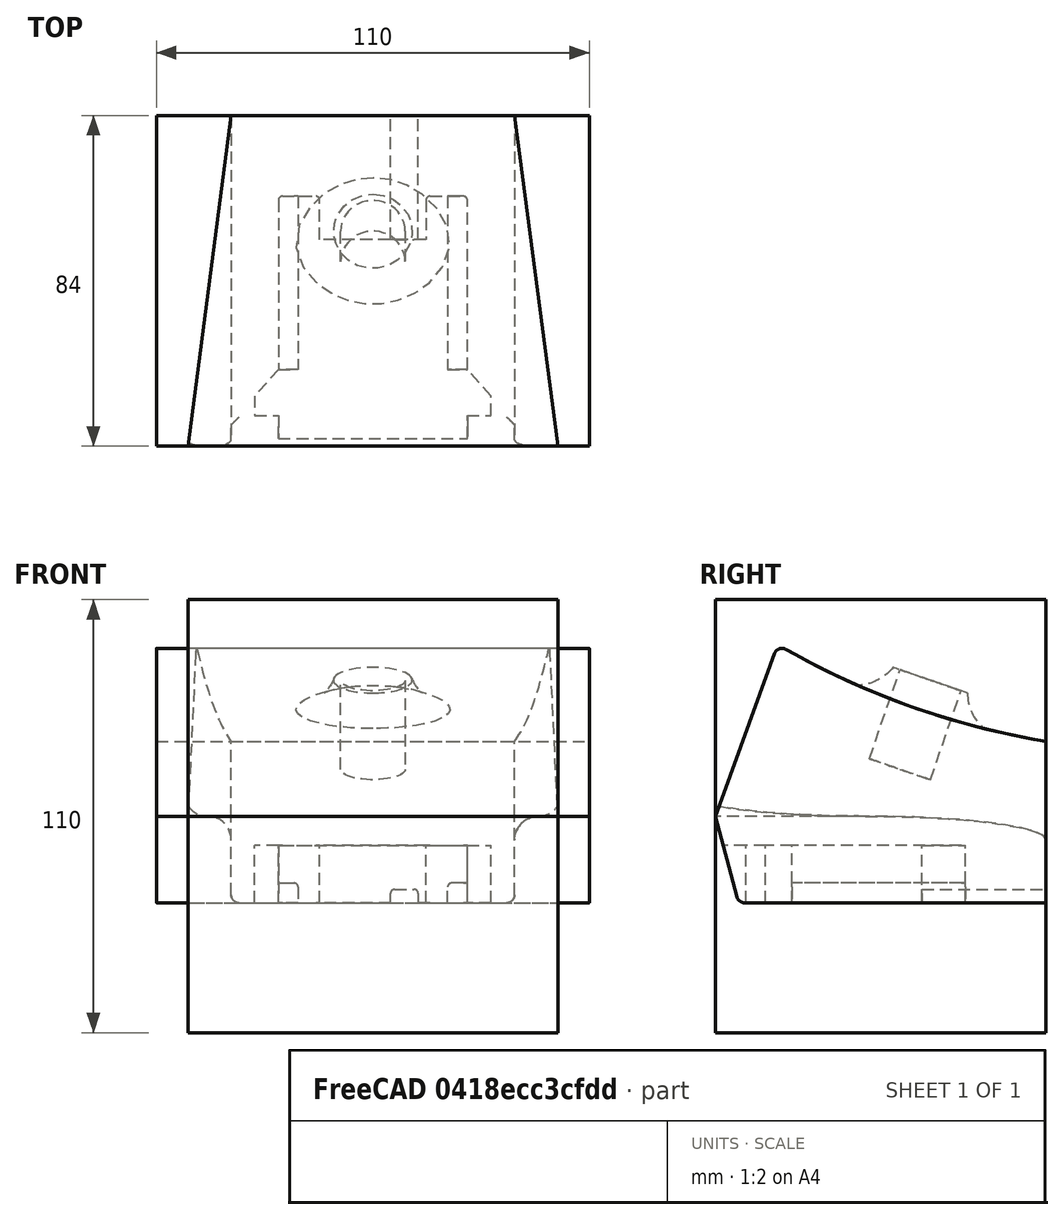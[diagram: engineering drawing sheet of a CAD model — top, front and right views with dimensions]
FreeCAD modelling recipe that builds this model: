
FCSTD DOCUMENT  (FreeCAD 0.19R24212 (Git))
Label: solder_station2
License: All rights reserved
LicenseURL: http://en.wikipedia.org/wiki/All_rights_reserved
objects: Sketcher::SketchObject×9, PartDesign::Pad×4, PartDesign::Body×3, PartDesign::Pocket×3, Spreadsheet::Sheet×1, Mesh::Feature×1, PartDesign::Boolean×1, PartDesign::Revolution×1, App::Part×1
note: 29 computed .brp shape members not serialized (recipe doc carries the construction recipe); baked Part::Feature solids carry a one-line shape summary decoded from their .brp

FEATURE [Sketcher::SketchObject] Sketch  label="RearSupport"
  AttachmentOffset = pos=(0,0,-42) rot=(0,0,1;0rad)
  FullyConstrained = true
  MapMode = 5
  Placement = pos=(-42,9.3e-15,-9.3e-15) rot=(0.57735,0.57735,0.57735;2.0944rad)
  Support = -> [YZ_Plane]
  expr: Constraints[44] = 3
  expr: Constraints[16] = <<param>>.rear_width
  expr: Constraints[52] = <<param>>.wall * 2
  expr: Constraints[56] = <<param>>.wall * 2
  expr: Constraints[15] = Spreadsheet.radius_big
  expr: .AttachmentOffset.Base.z = -Spreadsheet.mid_depth / 2
  expr: Constraints[18] = <<param>>.rear_height
  expr: Constraints[17] = <<param>>.rear_width / 2
  expr: Constraints[55] = <<param>>.wall * 2
  expr: Constraints[53] = <<param>>.wall * 2
  expr: Constraints[54] = <<param>>.wall * 2
  expr: Constraints[57] = <<param>>.wall * 2
  sketch-geometry (24):
    g0: LineSegment StartX=-30 StartY=41 StartZ=0 EndX=30 EndY=41 EndZ=0
    g1: LineSegment StartX=36 StartY=35 StartZ=0 EndX=36 EndY=6 EndZ=0
    g2: LineSegment StartX=30 StartY=0 StartZ=0 EndX=-30 EndY=0 EndZ=0
    g3: LineSegment StartX=-36 StartY=6 StartZ=0 EndX=-36 EndY=35 EndZ=0
    g4: ArcOfCircle CenterX=-30 CenterY=35 CenterZ=0 NormalX=0 NormalY=0 NormalZ=1 AngleXU=0 Radius=6 StartAngle=1.5708 EndAngle=3.14159
    g5: ArcOfCircle CenterX=30 CenterY=35 CenterZ=0 NormalX=0 NormalY=0 NormalZ=1 AngleXU=0 Radius=6 StartAngle=-9e-16 EndAngle=1.5708
    g6: ArcOfCircle CenterX=30 CenterY=6 CenterZ=0 NormalX=0 NormalY=0 NormalZ=1 AngleXU=0 Radius=6 StartAngle=4.71239 EndAngle=6.28319
    g7: ArcOfCircle CenterX=-30 CenterY=6 CenterZ=0 NormalX=0 NormalY=0 NormalZ=1 AngleXU=0 Radius=6 StartAngle=3.14159 EndAngle=4.71239
    g8: LineSegment StartX=-26.6 StartY=34.6 StartZ=0 EndX=-9.4 EndY=34.6 EndZ=0
    g9: LineSegment StartX=29.6 StartY=31.6 StartZ=0 EndX=29.6 EndY=9.4 EndZ=0
    g10: LineSegment StartX=26.6 StartY=6.4 StartZ=0 EndX=9.4 EndY=6.4 EndZ=0
    g11: LineSegment StartX=-29.6 StartY=9.4 StartZ=0 EndX=-29.6 EndY=31.6 EndZ=0
    g12: LineSegment StartX=-6.4 StartY=31.6 StartZ=0 EndX=-6.4 EndY=9.4 EndZ=0
    g13: LineSegment StartX=6.4 StartY=31.6 StartZ=0 EndX=6.4 EndY=9.4 EndZ=0
    g14: LineSegment StartX=9.4 StartY=34.6 StartZ=0 EndX=26.6 EndY=34.6 EndZ=0
    g15: LineSegment StartX=-9.4 StartY=6.4 StartZ=0 EndX=-26.6 EndY=6.4 EndZ=0
    g16: ArcOfCircle CenterX=-9.4 CenterY=31.6 CenterZ=0 NormalX=0 NormalY=0 NormalZ=1 AngleXU=0 Radius=3 StartAngle=4e-16 EndAngle=1.5708
    g17: ArcOfCircle CenterX=9.4 CenterY=31.6 CenterZ=0 NormalX=0 NormalY=0 NormalZ=1 AngleXU=0 Radius=3 StartAngle=1.5708 EndAngle=3.14159
    g18: ArcOfCircle CenterX=-9.4 CenterY=9.4 CenterZ=0 NormalX=0 NormalY=0 NormalZ=1 AngleXU=0 Radius=3 StartAngle=4.71239 EndAngle=6.28319
    g19: ArcOfCircle CenterX=9.4 CenterY=9.4 CenterZ=0 NormalX=0 NormalY=0 NormalZ=1 AngleXU=0 Radius=3 StartAngle=3.14159 EndAngle=4.71239
    g20: ArcOfCircle CenterX=-26.6 CenterY=31.6 CenterZ=0 NormalX=0 NormalY=0 NormalZ=1 AngleXU=0 Radius=3 StartAngle=1.5708 EndAngle=3.14159
    g21: ArcOfCircle CenterX=-26.6 CenterY=9.4 CenterZ=0 NormalX=0 NormalY=0 NormalZ=1 AngleXU=0 Radius=3 StartAngle=3.14159 EndAngle=4.71239
    g22: ArcOfCircle CenterX=26.6 CenterY=31.6 CenterZ=0 NormalX=0 NormalY=0 NormalZ=1 AngleXU=0 Radius=3 StartAngle=2e-16 EndAngle=1.5708
    g23: ArcOfCircle CenterX=26.6 CenterY=9.4 CenterZ=0 NormalX=0 NormalY=0 NormalZ=1 AngleXU=0 Radius=3 StartAngle=4.71239 EndAngle=6.28319
  constraints (58):
    c: Horizontal(g0)
    c: Horizontal(g2)
    c: Vertical(g1)
    c: Vertical(g3)
    c: Tangent(g3,g4) = 1.5708
    c: Tangent(g0,g4) = 1.5708
    c: Tangent(g0,g5) = 1.5708
    c: Tangent(g1,g5) = 1.5708
    c: Tangent(g1,g6) = 1.5708
    c: Tangent(g2,g6) = 1.5708
    c: Tangent(g2,g7) = 1.5708
    c: Tangent(g3,g7) = 1.5708
    c: Equal(g4,g7)
    c: Equal(g7,g6)
    c: Equal(g6,g5)
    c: Radius(g4) = 6
    c: DistanceX(g3,g1) = 72
    c: DistanceX(g3,g-1) = 36
    c: DistanceY(g2,g0) = 41
    c: Horizontal(g8)
    c: Horizontal(g10)
    c: Vertical(g9)
    c: Vertical(g11)
    c: Vertical(g12)
    c: Vertical(g13)
    c: PointOnObject(g-1,g2)
    c: Tangent(g8,g14)
    c: Tangent(g10,g15)
    c: Tangent(g8,g16) = 1.5708
    c: Tangent(g12,g16) = 1.5708
    c: Tangent(g13,g17) = -1.5708
    c: Tangent(g14,g17) = 1.5708
    c: Tangent(g15,g18) = 1.5708
    c: Tangent(g12,g18) = 1.5708
    c: Tangent(g13,g19) = -1.5708
    c: Tangent(g10,g19) = 1.5708
    c: Tangent(g8,g20) = 1.5708
    c: Tangent(g11,g20) = 1.5708
    c: Tangent(g11,g21) = 1.5708
    c: Tangent(g15,g21) = 1.5708
    c: Tangent(g14,g22) = 1.5708
    c: Tangent(g9,g22) = 1.5708
    c: Tangent(g9,g23) = 1.5708
    c: Tangent(g10,g23) = 1.5708
    c: Radius(g17) = 3
    c: Equal(g20,g21)
    c: Equal(g21,g18)
    c: Equal(g18,g16)
    c: Equal(g16,g19)
    c: Equal(g19,g23)
    c: Equal(g23,g22)
    c: Equal(g22,g17)
    c: DistanceY(g-1,g15) = 6.4
    c: DistanceX(g3,g11) = 6.4
    c: DistanceX(g9,g1) = 6.4
    c: DistanceX(g12,g-1) = 6.4
    c: DistanceX(g-1,g13) = 6.4
    c: DistanceY(g14,g0) = 6.4
FEATURE [Spreadsheet::Sheet] Spreadsheet  label="param"
  cells = A1=Body; B2=top_depth; C2(top_depth)=70; B3=mid_depth; C3(mid_depth)=84; B4=bottom_depth; C4(bottom_depth)=75; B6=bottom_width; C6(bottom_width)=72; B7=bottom_height; C7(bottom_height)=22; B8=bottom_angle; C8(bottom_angle)=15; B10=rear_width; C10(rear_width)=72; B11=rear_height; C11(rear_height)=41; B13=center_width; C13(center_width)=80; B14=center_height; C14(center_height)=50; B16=front_width1; C16(front_width1)=91; D16=@top; E16=not used; B17=front_width2; C17(front_width2)=94; D17=@mid; B18=front_height; C18(front_height)=65; B19=front_wall; C19(front_wall)=5; B20=front_face; C20(front_face)=44; B21=front_angle; C21(front_angle)=20; B23=wall; C23(wall)=3.2; B24=radius_big; C24(radius_big)=6; B25=radius_small; C25(radius_small)=2; B26=arch; C26(arch)=200; A28=Button; B29=button_offset; C29(button_offset)=10; B30=button_inside_dia; C30(button_inside_dia)=20; B31=button_outside_dia; C31(button_outside_dia)=40; B32=button_height; C32(button_height)=27; B33=button_extension; C33(button_extension)=8; B34=button_fillet; C34(button_fillet)=12; B35=button_angle; C35(button_angle)=-19; B36=button_hole; C36(button_hole)=16.4; B37=button_hole_center; C37(button_hole_center)=-0.5; A38=Battery Cuts; B39=batt_carveout; C39(batt_carveout)=14.6; B40=batt_rail; C40(batt_rail)=5; B41=batt_rail_length; C41(batt_rail_length)=44; A43=Terminals; B44=terminal_width; B45=terminal_height; A47=Box Interior
FEATURE [Sketcher::SketchObject] Sketch008  label="SketchButtonHole"
  AttachmentOffset = pos=(0,-0.5,27) rot=(1,0,0;-0.331613rad)
  FullyConstrained = true
  MapMode = 5
  Placement = pos=(0,-0.5,27) rot=(1,0,0;5.95157rad)
  Support = -> [XY_Plane004]
  expr: .AttachmentOffset.Base.z = <<param>>.button_height
  expr: Constraints[0] = <<param>>.button_hole
  expr: .AttachmentOffset.Base.y = <<param>>.button_hole_center
  expr: .AttachmentOffset.Rotation.Angle = <<param>>.button_angle
  expr: Constraints[2] = <<param>>.button_offset
  sketch-geometry (1):
    g0: Circle CenterX=0 CenterY=10 CenterZ=0 NormalX=0 NormalY=0 NormalZ=1 AngleXU=0 Radius=8.2
  constraints (3):
    c: Diameter(g0) = 16.4
    c: PointOnObject(g0,g-2)
    c: DistanceY(g-1,g0) = 10
FEATURE [Mesh::Feature] M18_soldering_case
  Placement = pos=(48,-41,-22) rot=(0,0.707107,0.707107;3.14159rad)
FEATURE [Sketcher::SketchObject] Sketch012  label="SketchSide"
  FullyConstrained = true
  MapMode = 5
  Placement = pos=(0,0,0) rot=(0.57735,0.57735,0.57735;2.0944rad)
  Support = -> [YZ_Plane002]
  expr: Constraints[21] = 90 - <<param>>.bottom_angle
  expr: Constraints[20] = <<param>>.radius_small
  expr: Constraints[19] = <<param>>.bottom_height
  expr: Constraints[8] = <<param>>.arch
  expr: Constraints[6] = <<param>>.rear_height - <<param>>.bottom_height
  expr: Constraints[11] = <<param>>.front_face
  expr: Constraints[7] = <<param>>.radius_small
  expr: Constraints[22] = 90 - <<param>>.front_angle
  expr: Constraints[9] = <<param>>.mid_depth
  sketch-geometry (8):
    g0: LineSegment StartX=42 StartY=0 StartZ=0 EndX=42 EndY=19 EndZ=0
    g1: LineSegment StartX=-42 StartY=0 StartZ=0 EndX=-26.9511 EndY=41.3465 EndZ=0
    g2: ArcOfCircle CenterX=-25.0717 CenterY=40.6624 CenterZ=0 NormalX=0 NormalY=0 NormalZ=1 AngleXU=0 Radius=2 StartAngle=1.05429 EndAngle=2.79253
    g3: ArcOfCircle CenterX=74.6859 CenterY=216.311 CenterZ=0 NormalX=0 NormalY=0 NormalZ=1 AngleXU=0 Radius=200 StartAngle=4.19588 EndAngle=4.54822
    g4: LineSegment StartX=-42 StartY=0 StartZ=0 EndX=-36.5023 EndY=-20.5176 EndZ=0
    g5: LineSegment StartX=-34.5705 StartY=-22 StartZ=0 EndX=42 EndY=-22 EndZ=0
    g6: LineSegment StartX=42 StartY=-22 StartZ=0 EndX=42 EndY=0 EndZ=0
    g7: ArcOfCircle CenterX=-34.5705 CenterY=-20 CenterZ=0 NormalX=0 NormalY=0 NormalZ=1 AngleXU=0 Radius=2 StartAngle=3.4034 EndAngle=4.71239
  constraints (25):
    c: PointOnObject(g1,g-1)
    c: Vertical(g0)
    c: Coincident(g2,g1)
    c: Coincident(g3,g0)
    c: Tangent(g3,g2) = 1.5708
    c: Symmetric(g1,g0,g-2)
    c: DistanceY(g0,g0) = 19
    c: Radius(g2) = 2
    c: Radius(g3) = 200
    c: DistanceX(g1,g0) = 84
    c: Tangent(g2,g1)
    c: Distance(g1) = 44
    c: Horizontal(g5)
    c: Coincident(g6,g5)
    c: Vertical(g6)
    c: Coincident(g7,g4)
    c: Coincident(g7,g5)
    c: Tangent(g7,g5)
    c: Tangent(g7,g4)
    c: DistanceY(g5,g-1) = 22
    c: Radius(g7) = 2
    c: Angle(g4,g-1) = 1.309
    c: Angle(g-1,g1) = 1.22173
    c: Coincident(g4,g1)
    c: Coincident(g6,g0)
FEATURE [PartDesign::Pad] Pad  label="PadSide"
  Direction = (1,1,1)
  Length = 110
  Length2 = 100
  Midplane = true
  Placement = pos=(0,0,0) rot=(0.57735,0.57735,0.57735;2.0944rad)
  Profile = -> Sketch012
  Type = 0
FEATURE [PartDesign::Body] Body001  label="BodySide"
  Group = -> [Sketch012,Pad]
  Origin = -> Origin002
  Tip = -> Pad
FEATURE [Sketcher::SketchObject] Sketch013  label="SketchTop"
  FullyConstrained = true
  MapMode = 5
  Support = -> [XY_Plane003]
  expr: Constraints[4] = <<param>>.front_width2
  expr: Constraints[6] = <<param>>.rear_width
  expr: Constraints[8] = <<param>>.mid_depth
  expr: Constraints[9] = <<param>>.mid_depth / 2
  sketch-geometry (4):
    g0: LineSegment StartX=36 StartY=42 StartZ=0 EndX=-36 EndY=42 EndZ=0
    g1: LineSegment StartX=-36 StartY=42 StartZ=0 EndX=-47 EndY=-42 EndZ=0
    g2: LineSegment StartX=-47 StartY=-42 StartZ=0 EndX=47 EndY=-42 EndZ=0
    g3: LineSegment StartX=47 StartY=-42 StartZ=0 EndX=36 EndY=42 EndZ=0
  constraints (10):
    c: Coincident(g0,g1)
    c: Coincident(g1,g2)
    c: Coincident(g2,g3)
    c: Coincident(g3,g0)
    c: DistanceX(g1,g2) = 94
    c: Symmetric(g2,g1,g-2)
    c: DistanceX(g0,g0) = 72
    c: Symmetric(g0,g0,g-2)
    c: DistanceY(g2,g0) = 84
    c: DistanceY(g2,g-1) = 42
FEATURE [PartDesign::Pad] Pad001  label="PadTop"
  Direction = (1,1,1)
  Length = 110
  Length2 = 100
  Midplane = true
  Profile = -> Sketch013
  Type = 0
FEATURE [PartDesign::Body] Body002  label="BodyTop"
  Group = -> [Sketch013,Pad001]
  Origin = -> Origin003
  Tip = -> Pad001
FEATURE [Sketcher::SketchObject] Sketch017  label="SketchFront"
  FullyConstrained = true
  MapMode = 5
  Placement = pos=(0,0,0) rot=(1,0,0;1.5708rad)
  Support = -> [XZ_Plane004]
  expr: Constraints[37] = <<param>>.front_height
  expr: Constraints[35] = <<param>>.front_width2
  expr: Constraints[34] = <<param>>.front_width1
  expr: Constraints[33] = <<param>>.bottom_width
  expr: Constraints[38] = <<param>>.bottom_height
  expr: Constraints[29] = <<param>>.radius_big
  expr: Constraints[28] = <<param>>.radius_small
  sketch-geometry (12):
    g0: LineSegment StartX=-34 StartY=-22 StartZ=0 EndX=34 EndY=-22 EndZ=0
    g1: LineSegment StartX=36 StartY=-20 StartZ=0 EndX=36 EndY=-6.00003 EndZ=0
    g2: LineSegment StartX=-36 StartY=-20 StartZ=0 EndX=-36 EndY=-6 EndZ=0
    g3: ArcOfCircle CenterX=-42 CenterY=-6 CenterZ=0 NormalX=0 NormalY=0 NormalZ=1 AngleXU=0 Radius=6 StartAngle=3.32288e-09 EndAngle=1.5708
    g4: ArcOfCircle CenterX=42 CenterY=-6 CenterZ=0 NormalX=0 NormalY=0 NormalZ=1 AngleXU=0 Radius=6 StartAngle=1.5708 EndAngle=3.1416
    g5: ArcOfCircle CenterX=42 CenterY=6 CenterZ=0 NormalX=0 NormalY=0 NormalZ=1 AngleXU=0 Radius=6 StartAngle=4.71239 EndAngle=5.6975
    g6: ArcOfCircle CenterX=-42 CenterY=6 CenterZ=0 NormalX=0 NormalY=0 NormalZ=1 AngleXU=0 Radius=6 StartAngle=3.72728 EndAngle=4.71239
    g7: LineSegment StartX=47 StartY=2.68339 StartZ=0 EndX=45.5 EndY=43 EndZ=0
    g8: LineSegment StartX=-45.5 StartY=43 StartZ=0 EndX=45.5 EndY=43 EndZ=0
    g9: ArcOfCircle CenterX=34 CenterY=-20 CenterZ=0 NormalX=0 NormalY=0 NormalZ=1 AngleXU=0 Radius=2 StartAngle=4.71239 EndAngle=6.28319
    g10: ArcOfCircle CenterX=-34 CenterY=-20 CenterZ=0 NormalX=0 NormalY=0 NormalZ=1 AngleXU=0 Radius=2 StartAngle=3.14159 EndAngle=4.71239
    g11: LineSegment StartX=-45.5 StartY=43 StartZ=0 EndX=-47 EndY=2.68339 EndZ=0
  constraints (39):
    c: Coincident(g8,g11)
    c: Coincident(g8,g7)
    c: Coincident(g11,g6)
    c: Coincident(g5,g7)
    c: Coincident(g0,g9)
    c: Coincident(g9,g1)
    c: Coincident(g0,g10)
    c: Coincident(g2,g10)
    c: Coincident(g2,g3)
    c: Coincident(g4,g1)
    c: Coincident(g4,g5)
    c: Coincident(g6,g3)
    c: Vertical(g1)
    c: Vertical(g2)
    c: PointOnObject(g4,g-1)
    c: Symmetric(g4,g3,g-2)
    c: Symmetric(g0,g0,g-2)
    c: Symmetric(g7,g8,g-2)
    c: Tangent(g9,g0)
    c: Tangent(g9,g1)
    c: Tangent(g10,g0)
    c: Tangent(g10,g2)
    c: Tangent(g3,g2)
    c: Tangent(g4,g1)
    c: Equal(g3,g6)
    c: Equal(g6,g4)
    c: Equal(g4,g5)
    c: Equal(g9,g10)
    c: Radius(g9) = 2
    c: Radius(g4) = 6
    c: Tangent(g4,g5)
    c: Tangent(g3,g6)
    c: Vertical(g4,g4)
    c: DistanceX(g2,g1) = 72
    c: DistanceX(g8,g8) = 91
    c: DistanceX(g6,g5) = 94
    c: Equal(g11,g7)
    c: DistanceY(g0,g7) = 65
    c: DistanceY(g0,g4) = 22
FEATURE [PartDesign::Pad] Pad003  label="PadFront"
  Direction = (1,1,1)
  Length = 110
  Length2 = 100
  Midplane = true
  Placement = pos=(0,0,0) rot=(1,0,0;1.5708rad)
  Profile = -> Sketch017
  Type = 0
FEATURE [PartDesign::Boolean] Boolean
  BaseFeature = -> Pad003
  Group = -> [Body002,Body001]
  Type = 2
FEATURE [Sketcher::SketchObject] Sketch018  label="SketchBat1"
  AttachmentOffset = pos=(0,0,-22) rot=(0,0,1;0rad)
  FullyConstrained = true
  MapMode = 5
  Placement = pos=(0,0,-22) rot=(0,0,1;0rad)
  Support = -> [XY_Plane004]
  expr: .AttachmentOffset.Base.z = -<<param>>.bottom_height
  sketch-geometry (21):
    g0: LineSegment StartX=-24 StartY=-44.2082 StartZ=0 EndX=24 EndY=-44.2082 EndZ=0
    g1: LineSegment StartX=24 StartY=-44.2082 StartZ=0 EndX=24 EndY=-34.2082 EndZ=0
    g2: LineSegment StartX=24 StartY=-34.2082 StartZ=0 EndX=30 EndY=-34.2082 EndZ=0
    g3: LineSegment StartX=30 StartY=-34.2082 StartZ=0 EndX=30 EndY=-29.2082 EndZ=0
    g4: LineSegment StartX=30 StartY=-29.2082 StartZ=0 EndX=24 EndY=-22.5 EndZ=0
    g5: LineSegment StartX=24 StartY=-22.5 StartZ=0 EndX=24 EndY=20.5 EndZ=0
    g6: LineSegment StartX=13.5 StartY=20.5 StartZ=0 EndX=13.5 EndY=10.5 EndZ=0
    g7: LineSegment StartX=13.5 StartY=10.5 StartZ=0 EndX=-13.5 EndY=10.5 EndZ=0
    g8: LineSegment StartX=-13.5 StartY=10.5 StartZ=0 EndX=-13.5 EndY=20.5 EndZ=0
    g9: LineSegment StartX=-24 StartY=20.5 StartZ=0 EndX=-24 EndY=-22.5 EndZ=0
    g10: LineSegment StartX=-24 StartY=-22.5 StartZ=0 EndX=-30 EndY=-29.2082 EndZ=0
    g11: LineSegment StartX=-30 StartY=-29.2082 StartZ=0 EndX=-30 EndY=-34.2082 EndZ=0
    g12: LineSegment StartX=-30 StartY=-34.2082 StartZ=0 EndX=-24 EndY=-34.2082 EndZ=0
    g13: LineSegment StartX=-24 StartY=-34.2082 StartZ=0 EndX=-24 EndY=-44.2082 EndZ=0
    g14: Circle CenterX=0 CenterY=37.5 CenterZ=0 NormalX=0 NormalY=0 NormalZ=1 AngleXU=0 Radius=4
    g15: ArcOfCircle CenterX=-14.5 CenterY=20.5 CenterZ=0 NormalX=0 NormalY=0 NormalZ=1 AngleXU=0 Radius=1 StartAngle=4.17262e-08 EndAngle=1.5708
    g16: LineSegment StartX=-23 StartY=21.5 StartZ=0 EndX=-14.5 EndY=21.5 EndZ=0
    g17: LineSegment StartX=14.5 StartY=21.5 StartZ=0 EndX=23 EndY=21.5 EndZ=0
    g18: ArcOfCircle CenterX=-23 CenterY=20.5 CenterZ=0 NormalX=0 NormalY=0 NormalZ=1 AngleXU=0 Radius=1 StartAngle=1.5708 EndAngle=3.14159
    g19: ArcOfCircle CenterX=14.5 CenterY=20.5 CenterZ=0 NormalX=0 NormalY=0 NormalZ=1 AngleXU=0 Radius=1 StartAngle=1.5708 EndAngle=3.14159
    g20: ArcOfCircle CenterX=23 CenterY=20.5 CenterZ=0 NormalX=0 NormalY=0 NormalZ=1 AngleXU=0 Radius=0.999999 StartAngle=6.28318 EndAngle=7.85398
  constraints (65):
    c: Horizontal(g0)
    c: Coincident(g1,g0)
    c: Vertical(g1)
    c: Coincident(g2,g1)
    c: Horizontal(g2)
    c: Coincident(g3,g2)
    c: Coincident(g3,g4)
    c: Vertical(g5)
    c: Coincident(g6,g7)
    c: Coincident(g7,g8)
    c: Vertical(g8)
    c: Vertical(g9)
    c: Coincident(g10,g11)
    c: Vertical(g11)
    c: Coincident(g11,g12)
    c: Horizontal(g12)
    c: Coincident(g12,g13)
    c: Equal(g6,g8)
    c: Equal(g5,g9)
    c: Equal(g4,g10)
    c: Equal(g3,g11)
    c: Equal(g12,g2)
    c: Equal(g1,g13)
    c: Coincident(g13,g0)
    c: Vertical(g13)
    c: DistanceX(g7,g7) = 27
    c: Symmetric(g7,g6,g-2)
    c: Distance(g4) = 9
    c: Vertical(g3)
    c: DistanceY(g3,g3) = 5
    c: DistanceX(g2,g2) = 6
    c: DistanceY(g1,g1) = 10
    c: DistanceX(g0,g0) = 48
    c: PointOnObject(g14,g-2)
    c: Coincident(g9,g10)
    c: Coincident(g5,g4)
    c: Coincident(g15,g8)
    c: Coincident(g16,g15)
    c: Tangent(g15,g8)
    c: Horizontal(g16)
    c: Horizontal(g17)
    c: DistanceX(g9,g5) = 48
    c: Symmetric(g4,g9,g-2)
    c: Equal(g16,g17)
    c: Coincident(g18,g9)
    c: Coincident(g18,g16)
    c: Equal(g18,g15)
    c: Tangent(g18,g16)
    c: Tangent(g18,g9)
    c: DistanceY(g6,g17) = 11
    c: Vertical(g6)
    c: Coincident(g19,g6)
    c: Coincident(g19,g17)
    c: Coincident(g20,g17)
    c: Coincident(g20,g5)
    c: Tangent(g20,g17)
    c: Tangent(g20,g5)
    c: Tangent(g19,g6)
    c: Tangent(g19,g17)
    c: Equal(g15,g19)
    c: Radius(g19) = 1
    c: Radius(g14) = 4
    c: DistanceY(g15,g14) = 16
    c: DistanceY(g9,g16) = 44
    c: DistanceY(g-1,g14) = 37.5
FEATURE [PartDesign::Pocket] Pocket  label="PocketBatt"
  BaseFeature = -> Boolean
  Length = 14.6
  Length2 = 100
  Profile = -> Sketch018
  Reversed = true
  Type = 0
  expr: Length = Spreadsheet.batt_carveout
FEATURE [Sketcher::SketchObject] Sketch019  label="SketchBat2"
  AttachmentOffset = pos=(0,0,-21.5) rot=(0,0,1;0rad)
  FullyConstrained = true
  MapMode = 5
  Placement = pos=(0,21.5,4.8e-15) rot=(1,0,0;1.5708rad)
  Support = -> [XZ_Plane004]
  expr: Constraints[28] = 48.01mm
  expr: .AttachmentOffset.Base.z = -<<param>>.bottom_depth / 2 + 16
  expr: Constraints[26] = <<param>>.bottom_height
  expr: Constraints[29] = <<param>>.batt_rail
  expr: Constraints[27] = <<param>>.batt_rail
  sketch-geometry (10):
    g0: LineSegment StartX=-24.005 StartY=-17 StartZ=0 EndX=-20.005 EndY=-17 EndZ=0
    g1: LineSegment StartX=-19.005 StartY=-22 StartZ=0 EndX=-24.005 EndY=-22 EndZ=0
    g2: LineSegment StartX=-24.005 StartY=-22 StartZ=0 EndX=-24.005 EndY=-17 EndZ=0
    g3: LineSegment StartX=24.005 StartY=-17 StartZ=0 EndX=20.005 EndY=-17 EndZ=0
    g4: LineSegment StartX=19.005 StartY=-22 StartZ=0 EndX=24.005 EndY=-22 EndZ=0
    g5: LineSegment StartX=24.005 StartY=-22 StartZ=0 EndX=24.005 EndY=-17 EndZ=0
    g6: LineSegment StartX=-19.005 StartY=-18 StartZ=0 EndX=-19.005 EndY=-22 EndZ=0
    g7: ArcOfCircle CenterX=20.005 CenterY=-18 CenterZ=0 NormalX=0 NormalY=0 NormalZ=1 AngleXU=0 Radius=1 StartAngle=1.5708 EndAngle=3.1416
    g8: LineSegment StartX=19.005 StartY=-22 StartZ=0 EndX=19.005 EndY=-18 EndZ=0
    g9: ArcOfCircle CenterX=-20.005 CenterY=-18 CenterZ=0 NormalX=0 NormalY=0 NormalZ=1 AngleXU=0 Radius=1 StartAngle=6.28318 EndAngle=7.85398
  constraints (30):
    c: Coincident(g1,g2)
    c: Coincident(g2,g0)
    c: Horizontal(g0)
    c: Horizontal(g1)
    c: Vertical(g2)
    c: Coincident(g4,g5)
    c: Coincident(g5,g3)
    c: Horizontal(g3)
    c: Horizontal(g4)
    c: Vertical(g5)
    c: Coincident(g6,g1)
    c: Vertical(g6)
    c: Equal(g1,g4)
    c: Tangent(g3,g7) = -1.5708
    c: Coincident(g8,g4)
    c: Vertical(g8)
    c: Coincident(g7,g8)
    c: Coincident(g9,g0)
    c: Coincident(g9,g6)
    c: Equal(g6,g8)
    c: Tangent(g7,g8)
    c: Tangent(g9,g6)
    c: Tangent(g9,g0)
    c: Equal(g9,g7)
    c: Radius(g9) = 1
    c: Symmetric(g1,g4,g-2)
    c: DistanceY(g1,g-1) = 22
    c: DistanceY(g4,g3) = 5
    c: DistanceX(g1,g4) = 48.01
    c: DistanceX(g4,g4) = 5
FEATURE [PartDesign::Pad] Pad004  label="PadRail"
  BaseFeature = -> Pocket
  Direction = (1,1,1)
  Length = 44
  Length2 = 100
  Profile = -> Sketch019
  Type = 0
  expr: Length = <<param>>.batt_rail_length
FEATURE [Sketcher::SketchObject] Sketch020  label="SketchNotch"
  FullyConstrained = true
  MapMode = 5
  Placement = pos=(0,0,0) rot=(1,0,0;1.5708rad)
  Support = -> [XZ_Plane004]
  expr: Constraints[6] = <<param>>.bottom_height
  sketch-geometry (6):
    g0: LineSegment StartX=5.5 StartY=-18.6 StartZ=0 EndX=10.5 EndY=-18.6 EndZ=0
    g1: LineSegment StartX=11.5 StartY=-19.6 StartZ=0 EndX=11.5 EndY=-22 EndZ=0
    g2: LineSegment StartX=11.5 StartY=-22 StartZ=0 EndX=4.5 EndY=-22 EndZ=0
    g3: LineSegment StartX=4.5 StartY=-22 StartZ=0 EndX=4.5 EndY=-19.6 EndZ=0
    g4: ArcOfCircle CenterX=5.5 CenterY=-19.6 CenterZ=0 NormalX=0 NormalY=0 NormalZ=1 AngleXU=0 Radius=1 StartAngle=1.5708 EndAngle=3.14159
    g5: ArcOfCircle CenterX=10.5 CenterY=-19.6 CenterZ=0 NormalX=0 NormalY=0 NormalZ=1 AngleXU=0 Radius=1 StartAngle=7e-16 EndAngle=1.5708
  constraints (16):
    c: Coincident(g1,g2)
    c: Coincident(g2,g3)
    c: Horizontal(g0)
    c: Horizontal(g2)
    c: Vertical(g1)
    c: Vertical(g3)
    c: DistanceY(g2,g-1) = 22
    c: Tangent(g3,g4) = 1.5708
    c: Tangent(g0,g4) = 1.5708
    c: Tangent(g0,g5) = 1.5708
    c: Tangent(g1,g5) = 1.5708
    c: Equal(g5,g4)
    c: Radius(g5) = 1
    c: DistanceY(g1,g0) = 3.4
    c: DistanceX(g2,g1) = 7
    c: DistanceX(g-1,g3) = 4.5
FEATURE [PartDesign::Pocket] Pocket001  label="PocketNotch"
  BaseFeature = -> Pad004
  Length = 5
  Length2 = 100
  Profile = -> Sketch020
  Type = 1
FEATURE [Sketcher::SketchObject] Sketch021
  AttachmentOffset = pos=(10,27,0) rot=(0,0,1;-0.331613rad)
  FullyConstrained = true
  MapMode = 5
  Placement = pos=(-3.8e-15,10,27) rot=(-0.502173,-0.70402,-0.502173;4.36843rad)
  Support = -> [YZ_Plane004]
  expr: .AttachmentOffset.Base.x = <<param>>.button_offset
  expr: .AttachmentOffset.Rotation.Angle = <<param>>.button_angle
  expr: .AttachmentOffset.Base.y = <<param>>.button_height
  expr: Constraints[11] = <<param>>.button_fillet
  expr: Constraints[10] = <<param>>.button_outside_dia / 2
  expr: Constraints[9] = <<param>>.button_inside_dia / 2
  expr: Constraints[8] = <<param>>.button_extension
  sketch-geometry (4):
    g0: ArcOfCircle CenterX=21.34 CenterY=11.925 CenterZ=0 NormalX=0 NormalY=0 NormalZ=1 AngleXU=0 Radius=12 StartAngle=3.4748 EndAngle=4.60049
    g1: LineSegment StartX=0 StartY=2.13e-14 StartZ=0 EndX=0 EndY=8 EndZ=0
    g2: LineSegment StartX=0 StartY=8 StartZ=0 EndX=10 EndY=8 EndZ=0
    g3: LineSegment StartX=0 StartY=2.13e-14 StartZ=0 EndX=20 EndY=2.13e-14 EndZ=0
  constraints (12):
    c: Coincident(g1,g-1)
    c: PointOnObject(g1,g-2)
    c: Coincident(g2,g1)
    c: Coincident(g2,g0)
    c: Horizontal(g2)
    c: Coincident(g3,g1)
    c: Coincident(g3,g0)
    c: Horizontal(g3)
    c: DistanceY(g1,g1) = 8
    c: DistanceX(g2,g2) = 10
    c: DistanceX(g3,g3) = 20
    c: Radius(g0) = 12
FEATURE [PartDesign::Revolution] Revolution
  Angle = 360
  Axis = (-1e-16,0.325568,0.945519)
  Base = (-3.8e-15,10,27)
  BaseFeature = -> Pocket001
  Profile = -> Sketch021
  ReferenceAxis = -> Sketch021 [V_Axis]
  Reversed = true
FEATURE [PartDesign::Pocket] Pocket002
  BaseFeature = -> Revolution
  Length = 25
  Length2 = 100
  Midplane = true
  Profile = -> Sketch008
  Type = 0
FEATURE [PartDesign::Body] Body003  label="BodyFront"
  Group = -> [Sketch017,Pad003,Boolean,Sketch018,Pocket,Sketch019,Pad004,Sketch020,Pocket001,Sketch008,Sketch021,Revolution,Pocket002]
  Origin = -> Origin004
  Tip = -> Pocket002
FEATURE [App::Part] Part
  Group = -> [Body003,Sketch]
  Origin = -> Origin
